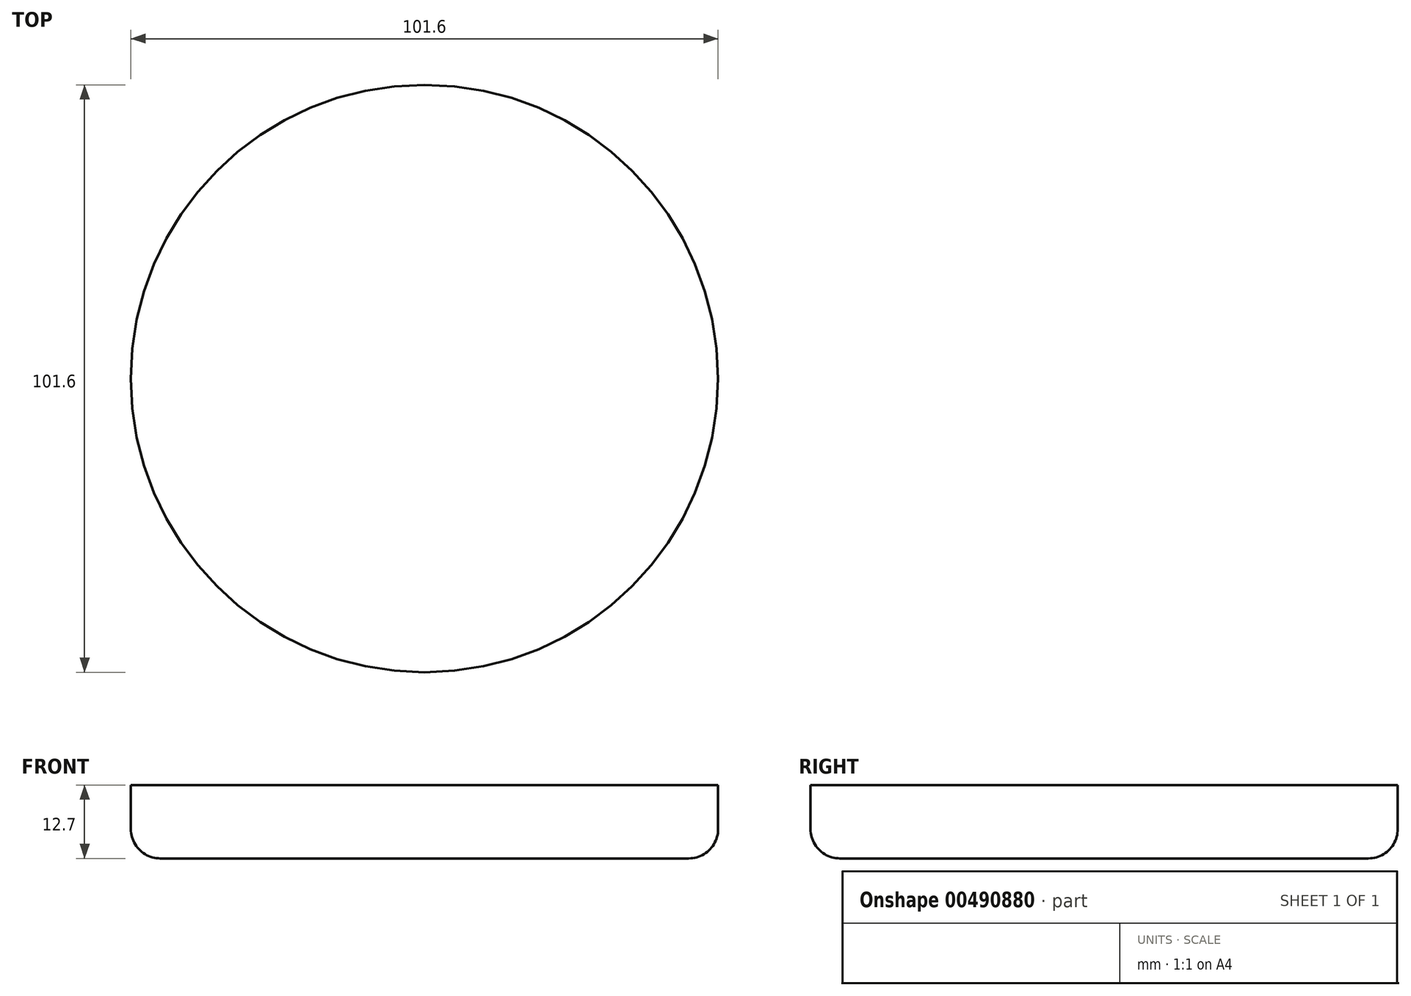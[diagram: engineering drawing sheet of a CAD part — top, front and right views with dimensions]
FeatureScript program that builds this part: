
annotation { "Feature Type Name" : "Feature", "Feature Type Description" : "" }
export const myFeature = defineFeature(function(context is Context, id is Id, definition is map)
    precondition{}
    {
        {
            var Q0;
            Q0=qCreatedBy(makeId("Front.planeOp"),FACE);
            var sketch = newSketch(context, id + "F0", { "sketchPlane" : qUnion([Q0])});
            skLineSegment(sketch, "E0.bottom", {"start": v(-25.4, -6.35) * mm, "end": v(25.4, -6.35) * mm});
            skLineSegment(sketch, "E0.top", {"start": v(-25.4, 6.35) * mm, "end": v(25.4, 6.35) * mm});
            skLineSegment(sketch, "E0.left", {"start": v(-25.4, -6.35) * mm, "end": v(-25.4, 6.35) * mm});
            skLineSegment(sketch, "E0.right", {"start": v(25.4, -6.35) * mm, "end": v(25.4, 6.35) * mm});
            skPoint(sketch, "E0.middle", {"position": v(0, 0) * mm});
            skSolve(sketch);
        }
        {
            var Q0;
            Q0=makeQuery(id+"F0.imprint","IMPRINT",FACE,{"disambiguationData":[TD([[makeQuery(id+"F0.imprint","IMPRINT",EDGE,{"derivedFrom":sQuery(id+"F0.wireOp",EDGE,"E0.bottom")}),1.0]])]});
            var Q1;
            Q1=sQuery(id+"F0.wireOp",EDGE,"E0.right");
            revolve(context, id + "F1", {"entities" : qUnion([Q0]), "axis" : qUnion([Q1]), "revolveType" : RevolveType.FULL});
        }
        {
            var Q0;
            Q0=makeQuery(id+"F1.opRevolve","SWEPT_EDGE",EDGE,{"disambiguationData":[OSD([sQuery(id+"F0.wireOp",EDGE,"E0.bottom"),sQuery(id+"F0.wireOp",EDGE,"E0.left")])]});
            fillet(context, id + "F2", {"entities" : qUnion([Q0]), "radius" : 5.08 * mm, "tangentPropagation" : true, "allowEdgeOverflow" : false});
        }
    });
